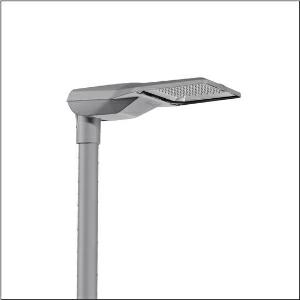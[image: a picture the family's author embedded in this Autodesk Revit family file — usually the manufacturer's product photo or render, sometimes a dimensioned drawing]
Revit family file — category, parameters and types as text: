
# Revit family: streetlight_sl_21_iq_midi___stw1_0a_5xe3e41d08nb_e017
name_source: partatom
category: Lighting Fixtures
units: mm (PartAtom-declared; Revit-internal decimal feet)

## family parameters
Cut with Voids When Loaded = No
Host = Face
Light Source = No
Part Type = Normal
Room Calculation Point = No
Round Connector Dimension = Use Diameter
Shared = No

## types (1)
- --- (1 x LED, 24250 lm, 155.5 W, 4000K)
    Apparent Load = 155 VA
    CIE Flux Codes = 39 75 98 100 100
    Color Rendering = 70
    Color Temperature = 4000K
    Default Elevation = 1800 mm
    Description = Streetlight SL 21 iQ midi, mast luminaire, primary light control with lens, of PMMA, primary optical cover: cover, of toughened safety glass, transparent, light distribution: STW1.0a, light emission: direct distribution, primary light characteristic: asymmetric, installation type: post-top, side-entry, LED, High Power LED, rated luminous flux: 24.250lm, luminous efficacy: 156lm/W, light colour: 740, colour temperature: 4000K, control: Auto-Match, Temp-Guard, Lumen-Switch, Night-Set, Smart-Wire, Light-Fading, Desk-Remote (wireless, voltage-free reading and setting of iQ features in the workshop via application-optimized NFC function/RFID function), optimised constant luminous flux control (CLO 2.0), presetting dimming linear, mains connection: 230..240V, AC, 50/60Hz, start of lifetime: 156W, end of service life: 162W, reduction: 69W, luminaire housing, of diecast aluminium, powder-coated, Siteco® metallic grey (DB 702S), corrosivity category C5 mid according to DIN EN ISO 12944, please order mast flange separately, inclination adjustable: 0°, 5°, 10°, 15°, sealing non-destructively replaceable, multi-level sealing system, length: 644mm, width: 335mm, height: 110mm, mast flange for spigot size: 42mm (side-entry): 5XC10008XM4, 60/48mm (side-entry/post-top): 5XC10108XM2, 76/60mm (side-entry/post-top): 5XC10108XM1, protection rating (complete): IP66, insulation class (complete): insulation class II (safety insulation), certification: CE, ENEC, ENEC+, VDE, impact resistance: IK09, permissible operating ambient temperature for outdoor applications: -40..+50°C, standard-compliant lighting for roads and squares, packaging unit: 1 piece

Light Distribution: STW1.0a
    Height = 111 mm
    Lamp = 1 x LED
    Lamp Light Flux = 24250 lm
    Lamp Power = 155.5 W
    Lamp count = 1
    Length = 644 mm
    Luminous efficacy = 156 lm/W
    Manufacturer = Siteco
    ModVariant = No
    Model = 5XE3E41D08NB
    Number of Poles = 1
    OnlyDefault = Yes
    Power Factor = 1
    Product Name = Streetlight SL 21 iQ midi | STW1.0a
    Product group = mast luminaire | pylon top
    ProductGroupID = 6100
    Protection Class = Protection class II
    Protection Degree = IP 66
    RLX_Detail_Level = 1
    RLX_Emergency_Light_Flux = 0 lm
    RLX_Emergency_Type = 0
    RLX_Emergency_Type_DB = No
    RlxData = <blob elided: 91225 chars, md5=daa87ba8>
    Socket = socket
    Standby Power = 0 W
    System Light Flux = 24250 lm
    System Power = 155 W
    Type Comments = factory setting: luminous flux: 100 % | dim-lin: 254 | 823 mA
    Type Image = l_1004298.jpg
    URL = http://relux.com
    VarID = @adj_102425
    Voltage = 0 V
    Weight = 0.00 kg
    Width = 336 mm

## geometry (parser evidence)
native form markers: Blend x4, Sweep x10
no freeform markers — native parametric forms only
